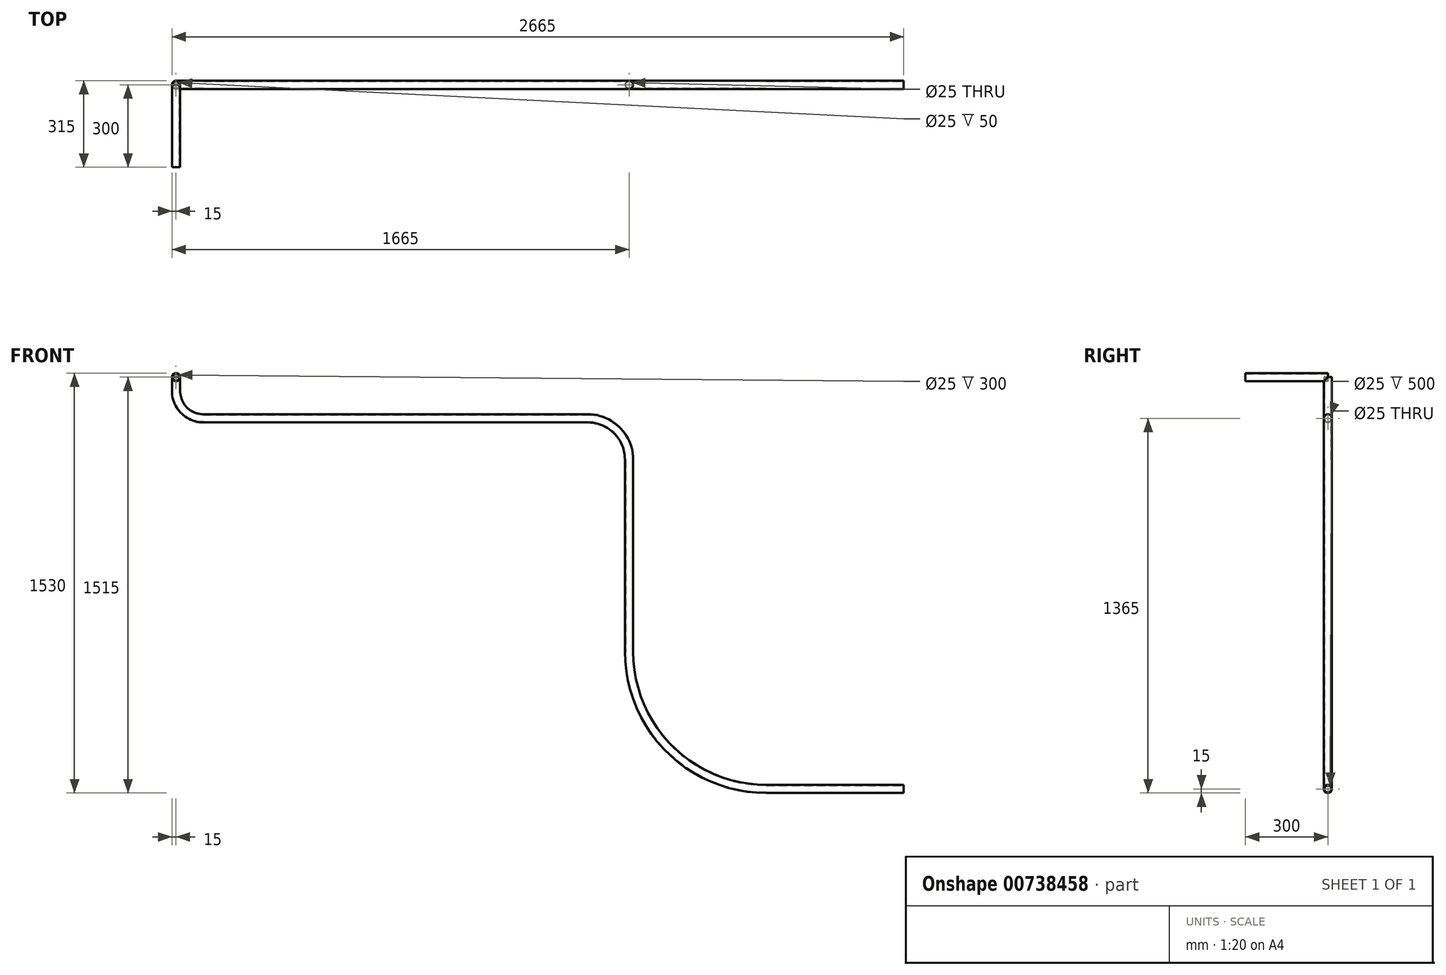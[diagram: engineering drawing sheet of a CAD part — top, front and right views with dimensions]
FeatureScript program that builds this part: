
annotation { "Feature Type Name" : "Feature", "Feature Type Description" : "" }
export const myFeature = defineFeature(function(context is Context, id is Id, definition is map)
    precondition{}
    {
        {
            var Q0;
            Q0=qCreatedBy(makeId("Front.planeOp"),FACE);
            var sketch = newSketch(context, id + "F0", { "sketchPlane" : qUnion([Q0])});
            skCircle(sketch, "E0", {"center": v(0, 0) * mm, "radius": 15 * mm});
            skCircle(sketch, "E1", {"center": v(0, 0) * mm, "radius": 12.5 * mm});
            skSolve(sketch);
        }
        {
            var Q0;
            Q0=makeQuery(id+"F0.imprint","IMPRINT",FACE,{"disambiguationData":[TD([[makeQuery(id+"F0.imprint","IMPRINT",EDGE,{"derivedFrom":sQuery(id+"F0.wireOp",EDGE,"E0")}),1.0]])]});
            extrude(context, id + "F1", {"entities" : qUnion([Q0]), "depth" : 300 * mm, "offsetDistance" : 25 * mm});
        }
        {
            var Q0;
            Q0=qCreatedBy(makeId("Top.planeOp"),FACE);
            var sketch = newSketch(context, id + "F2", { "sketchPlane" : qUnion([Q0])});
            skCircle(sketch, "E2", {"center": v(0, 0) * mm, "radius": 15 * mm});
            skCircle(sketch, "E3", {"center": v(0, 0) * mm, "radius": 12.5 * mm});
            skSolve(sketch);
        }
        {
            var Q0;
            Q0=qCreatedBy(makeId("Front.planeOp"),FACE);
            var sketch = newSketch(context, id + "F3", { "sketchPlane" : qUnion([Q0])});
            skLineSegment(sketch, "E4", {"start": v(1650, -300) * mm, "end": v(1650, -1000) * mm});
            skLineSegment(sketch, "E5", {"start": v(2150, -1500) * mm, "end": v(2650, -1500) * mm});
            skPoint(sketch, "E6.visualSharp", {"position": v(1650, -1500) * mm});
            skArc(sketch, "E6.filletArc", {"start": v(1650, -1000) * mm, "mid": v(1796.45, -1353.55) * mm, "end": v(2150, -1500) * mm});
            skLineSegment(sketch, "E7", {"start": v(1500, -150) * mm, "end": v(100, -150) * mm});
            skLineSegment(sketch, "E8", {"start": v(0, -50) * mm, "end": v(0, 0) * mm});
            skPoint(sketch, "E9.visualSharp", {"position": v(1650, -150) * mm});
            skArc(sketch, "E9.filletArc", {"start": v(1650, -300) * mm, "mid": v(1606.07, -193.93) * mm, "end": v(1500, -150) * mm});
            skPoint(sketch, "E10.visualSharp", {"position": v(0, -150) * mm});
            skArc(sketch, "E10.filletArc", {"start": v(0, -50) * mm, "mid": v(29.29, -120.71) * mm, "end": v(100, -150) * mm});
            skSolve(sketch);
        }
        {
            var Q0;
            Q0=makeQuery(id+"F2.imprint","IMPRINT",FACE,{"disambiguationData":[TD([[makeQuery(id+"F2.imprint","IMPRINT",EDGE,{"derivedFrom":sQuery(id+"F2.wireOp",EDGE,"E2")}),1.0]])]});
            var Q1;
            Q1=sQuery(id+"F3.wireOp",EDGE,"E8");
            var Q2;
            Q2=sQuery(id+"F3.wireOp",EDGE,"E10.filletArc");
            var Q3;
            Q3=sQuery(id+"F3.wireOp",EDGE,"E7");
            var Q4;
            Q4=sQuery(id+"F3.wireOp",EDGE,"E9.filletArc");
            var Q5;
            Q5=sQuery(id+"F3.wireOp",EDGE,"E4");
            var Q6;
            Q6=sQuery(id+"F3.wireOp",EDGE,"E6.filletArc");
            var Q7;
            Q7=sQuery(id+"F3.wireOp",EDGE,"E5");
            sweep(context, id + "F4", {"operationType" : NewBodyOperationType.ADD, "profiles" : qUnion([Q0]), "path" : qUnion([Q1, Q2, Q3, Q4, Q5, Q6, Q7])});
        }
    });
